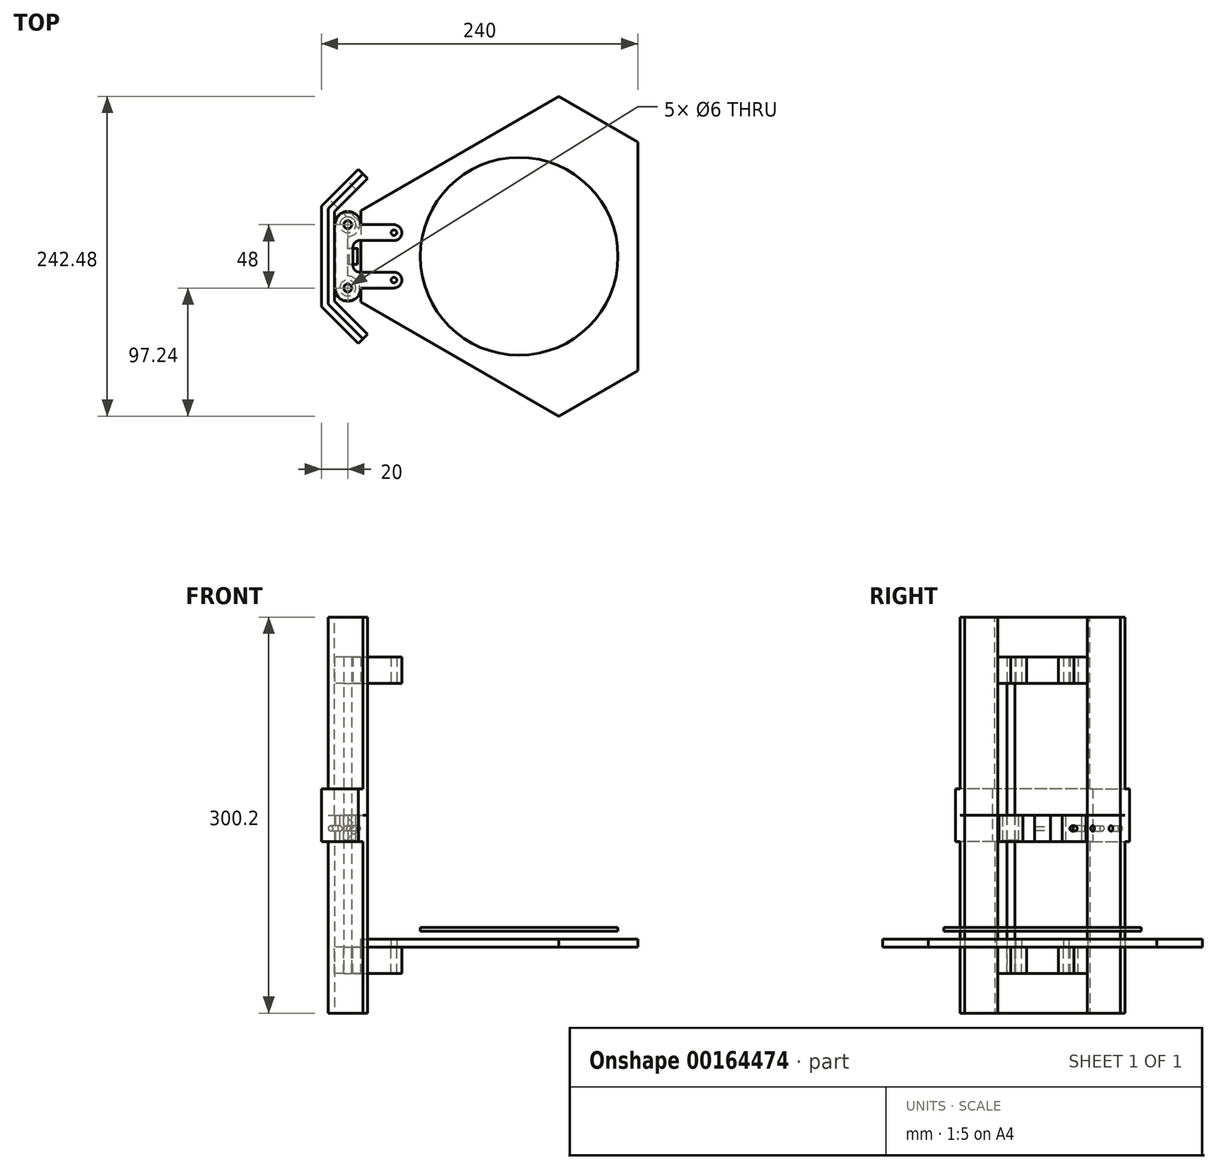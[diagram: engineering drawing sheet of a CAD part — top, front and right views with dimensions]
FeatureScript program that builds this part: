
annotation { "Feature Type Name" : "Feature", "Feature Type Description" : "" }
export const myFeature = defineFeature(function(context is Context, id is Id, definition is map)
    precondition{}
    {
        {
            var Q0;
            Q0=qCreatedBy(makeId("Top.planeOp"),FACE);
            var sketch = newSketch(context, id + "F0", { "sketchPlane" : qUnion([Q0])});
            skCircle(sketch, "E0", {"center": v(0, 0) * mm, "radius": 75 * mm});
            skSolve(sketch);
        }
        {
            var Q0;
            Q0=makeQuery(id+"F0.imprint","IMPRINT",FACE,{"disambiguationData":[TD([[makeQuery(id+"F0.imprint","IMPRINT",EDGE,{"derivedFrom":sQuery(id+"F0.wireOp",EDGE,"E0")}),1.0]])]});
            extrude(context, id + "F1", {"entities" : qUnion([Q0]), "depth" : 3 * mm});
        }
        {
            var Q0;
            Q0=qCreatedBy(makeId("Top.planeOp"),FACE);
            cPlane(context, id + "F2", {"entities" : qUnion([Q0]), "cplaneType" : CPlaneType.OFFSET, "offset" : 6 * mm, "oppositeDirection" : true, "width" : 150 * mm, "height" : 150 * mm});
        }
        {
            var Q0;
            Q0=qCreatedBy(id+"F2.planeOp",FACE);
            var sketch = newSketch(context, id + "F3", { "sketchPlane" : qUnion([Q0])});
            skLineSegment(sketch, "E1", {"start": v(30, 121.24) * mm, "end": v(-120, 34.64) * mm});
            skLineSegment(sketch, "E2", {"start": v(-120, 34.64) * mm, "end": v(-120, -34.64) * mm});
            skLineSegment(sketch, "E3", {"start": v(-120, 0) * mm, "end": v(0, 0) * mm, "construction": true});
            skLineSegment(sketch, "E4.1.0", {"start": v(30, -121.24) * mm, "end": v(90, -86.6) * mm});
            skLineSegment(sketch, "E4.1.1", {"start": v(-120, -34.64) * mm, "end": v(30, -121.24) * mm});
            skLineSegment(sketch, "E4.2.0", {"start": v(90, 86.6) * mm, "end": v(30, 121.24) * mm});
            skLineSegment(sketch, "E4.2.1", {"start": v(90, -86.6) * mm, "end": v(90, 86.6) * mm});
            skPoint(sketch, "E4.center", {"position": v(0, 0) * mm});
            skCircle(sketch, "E5", {"center": v(0, 0) * mm, "radius": 90 * mm, "construction": true});
            skSolve(sketch);
        }
        {
            var Q0;
            Q0=makeQuery(id+"F3.imprint","IMPRINT",FACE,{"disambiguationData":[TD([[makeQuery(id+"F3.imprint","IMPRINT",EDGE,{"derivedFrom":sQuery(id+"F3.wireOp",EDGE,"E1")}),1.0]])]});
            extrude(context, id + "F4", {"entities" : qUnion([Q0]), "oppositeDirection" : true, "depth" : 6 * mm});
        }
        {
            var Q0;
            Q0=makeQuery(id+"F4.opExtrude","CAP_FACE",FACE,{"disambiguationData":[OSD([sQuery(id+"F3.wireOp",EDGE,"E1"),sQuery(id+"F3.wireOp",EDGE,"E2"),sQuery(id+"F3.wireOp",EDGE,"E4.1.0"),sQuery(id+"F3.wireOp",EDGE,"E4.1.1"),sQuery(id+"F3.wireOp",EDGE,"E4.2.0"),sQuery(id+"F3.wireOp",EDGE,"E4.2.1")])],"isStart":false});
            var sketch = newSketch(context, id + "F5", { "sketchPlane" : qUnion([Q0])});
            skLineSegment(sketch, "E6", {"start": v(-120, 0) * mm, "end": v(-90, 0) * mm, "construction": true});
            skPoint(sketch, "E6.endSnap0", {"position": v(-120, 0) * mm});
            skLineSegment(sketch, "E7", {"start": v(-120, 18) * mm, "end": v(-95, 18) * mm, "construction": true});
            skArc(sketch, "E8.0.endCap", {"start": v(-95, 24) * mm, "mid": v(-89, 18) * mm, "end": v(-95, 12) * mm});
            skLineSegment(sketch, "E8.0.left", {"start": v(-120, 24) * mm, "end": v(-95, 24) * mm});
            skLineSegment(sketch, "E8.0.right", {"start": v(-119.48, 12) * mm, "end": v(-95, 12) * mm});
            skArc(sketch, "E9.MirrorCS", {"start": v(-95, -24) * mm, "mid": v(-89, -18) * mm, "end": v(-95, -12) * mm});
            skLineSegment(sketch, "E10.MirrorCS", {"start": v(-120, -24) * mm, "end": v(-95, -24) * mm});
            skLineSegment(sketch, "E11.MirrorCS", {"start": v(-119.48, -12) * mm, "end": v(-95, -12) * mm});
            skCircle(sketch, "E12", {"center": v(-95, 18) * mm, "radius": 2.1 * mm});
            skCircle(sketch, "E13", {"center": v(-95, -18) * mm, "radius": 2.1 * mm});
            skLineSegment(sketch, "E14", {"start": v(-140, 24) * mm, "end": v(-140, -24) * mm});
            skLineSegment(sketch, "E15", {"start": v(-126, 7) * mm, "end": v(-126, -7) * mm});
            skPoint(sketch, "E16.orphan", {"position": v(-120, -24) * mm});
            skPoint(sketch, "E17.MirrorCS.start.orphan", {"position": v(-119.48, -12) * mm});
            skLineSegment(sketch, "E18", {"start": v(-119.48, -12) * mm, "end": v(-121, -12) * mm});
            skLineSegment(sketch, "E19", {"start": v(-119.48, 12) * mm, "end": v(-121, 12) * mm});
            skArc(sketch, "E20", {"start": v(-121, 12) * mm, "mid": v(-124.54, 10.54) * mm, "end": v(-126, 7) * mm});
            skArc(sketch, "E21.MirrorCS", {"start": v(-121, -12) * mm, "mid": v(-124.54, -10.54) * mm, "end": v(-126, -7) * mm});
            skCircle(sketch, "E22", {"center": v(-130, -24) * mm, "radius": 3 * mm});
            skArc(sketch, "E23", {"start": v(-140, -24) * mm, "mid": v(-130, -34) * mm, "end": v(-120, -24) * mm});
            skCircle(sketch, "E24.MirrorC", {"center": v(-130, 24) * mm, "radius": 3 * mm});
            skArc(sketch, "E25.MirrorCS", {"start": v(-140, 24) * mm, "mid": v(-130, 34) * mm, "end": v(-120, 24) * mm});
            skSolve(sketch);
        }
        {
            var Q0;
            Q0 = qSketchRegion(id + "F5", true);
            extrude(context, id + "F6", {"entities" : qUnion([Q0]), "depth" : 20 * mm});
        }
        {
            var Q0;
            Q0=makeQuery(id+"F4.opExtrude","CAP_FACE",FACE,{"disambiguationData":[OSD([sQuery(id+"F3.wireOp",EDGE,"E1"),sQuery(id+"F3.wireOp",EDGE,"E2"),sQuery(id+"F3.wireOp",EDGE,"E4.1.0"),sQuery(id+"F3.wireOp",EDGE,"E4.1.1"),sQuery(id+"F3.wireOp",EDGE,"E4.2.0"),sQuery(id+"F3.wireOp",EDGE,"E4.2.1")])],"isStart":false});
            cPlane(context, id + "F7", {"entities" : qUnion([Q0]), "cplaneType" : CPlaneType.OFFSET, "offset" : 50 * mm, "width" : 150 * mm, "height" : 150 * mm});
        }
        {
            var Q0;
            Q0=qCreatedBy(id+"F7.planeOp",FACE);
            var sketch = newSketch(context, id + "F8", { "sketchPlane" : qUnion([Q0])});
            skLineSegment(sketch, "E26", {"start": v(-140, -34) * mm, "end": v(-140, 34) * mm});
            skLineSegment(sketch, "E27", {"start": v(-140, 34) * mm, "end": v(-115, 59) * mm});
            skLineSegment(sketch, "E28", {"start": v(-140, 0) * mm, "end": v(-105.12, 0) * mm, "construction": true});
            skLineSegment(sketch, "E29.MirrorCS", {"start": v(-140, -34) * mm, "end": v(-115, -59) * mm});
            skLineSegment(sketch, "E30.0", {"start": v(-145, 36.07) * mm, "end": v(-118.54, 62.54) * mm});
            skLineSegment(sketch, "E30.1", {"start": v(-145, -36.07) * mm, "end": v(-145, 36.07) * mm});
            skLineSegment(sketch, "E30.2", {"start": v(-145, -36.07) * mm, "end": v(-118.54, -62.54) * mm});
            skLineSegment(sketch, "E31", {"start": v(-115, 59) * mm, "end": v(-118.54, 62.54) * mm});
            skLineSegment(sketch, "E32", {"start": v(-115, -59) * mm, "end": v(-118.54, -62.54) * mm});
            skSolve(sketch);
        }
        {
            var Q0;
            Q0=makeQuery(id+"F8.imprint","IMPRINT",FACE,{"disambiguationData":[TD([[makeQuery(id+"F8.imprint","IMPRINT",EDGE,{"derivedFrom":sQuery(id+"F8.wireOp",EDGE,"E26")}),1.0]])]});
            extrude(context, id + "F9", {"entities" : qUnion([Q0]), "operationType" : NewBodyOperationType.ADD, "oppositeDirection" : true, "depth" : 150 * mm});
        }
        {
            var Q0;
            Q0=makeQuery(id+"F9.opExtrude","CAP_FACE",FACE,{"disambiguationData":[OSD([sQuery(id+"F8.wireOp",EDGE,"E26"),sQuery(id+"F8.wireOp",EDGE,"E27"),sQuery(id+"F8.wireOp",EDGE,"E29.MirrorCS"),sQuery(id+"F8.wireOp",EDGE,"E30.0"),sQuery(id+"F8.wireOp",EDGE,"E30.1"),sQuery(id+"F8.wireOp",EDGE,"E30.2"),sQuery(id+"F8.wireOp",EDGE,"E31"),sQuery(id+"F8.wireOp",EDGE,"E32")])],"isStart":false});
            cPlane(context, id + "F10", {"entities" : qUnion([Q0]), "cplaneType" : CPlaneType.OFFSET, "offset" : .1 * mm, "width" : 150 * mm, "height" : 150 * mm});
        }
        {
            var Q0;
            Q0=makeQuery(id+"F6.opExtrude","SWEPT_BODY",BODY,{"disambiguationData":[OSD([sQuery(id+"F5.wireOp",EDGE,"E8.0.endCap"),sQuery(id+"F5.wireOp",EDGE,"E8.0.left"),sQuery(id+"F5.wireOp",EDGE,"E8.0.right"),sQuery(id+"F5.wireOp",EDGE,"E9.MirrorCS"),sQuery(id+"F5.wireOp",EDGE,"E10.MirrorCS"),sQuery(id+"F5.wireOp",EDGE,"E11.MirrorCS"),sQuery(id+"F5.wireOp",EDGE,"E12"),sQuery(id+"F5.wireOp",EDGE,"E13"),sQuery(id+"F5.wireOp",EDGE,"E14"),sQuery(id+"F5.wireOp",EDGE,"E15"),sQuery(id+"F5.wireOp",EDGE,"E18"),sQuery(id+"F5.wireOp",EDGE,"E19"),sQuery(id+"F5.wireOp",EDGE,"E20"),sQuery(id+"F5.wireOp",EDGE,"E21.MirrorCS"),sQuery(id+"F5.wireOp",EDGE,"E22"),sQuery(id+"F5.wireOp",EDGE,"E23"),sQuery(id+"F5.wireOp",EDGE,"E24.MirrorC"),sQuery(id+"F5.wireOp",EDGE,"E25.MirrorCS")])]});
            var Q1;
            Q1=qCreatedBy(id+"F10.planeOp",FACE);
            mirror(context, id + "F11", {"entities" : qUnion([Q0]), "mirrorPlane" : qUnion([Q1])});
        }
        {
            var Q0;
            Q0=qCreatedBy(id+"F10.planeOp",FACE);
            var sketch = newSketch(context, id + "F12", { "sketchPlane" : qUnion([Q0])});
            skLineSegment(sketch, "E33.0", {"start": v(-150, -38.14) * mm, "end": v(-122.07, -66.07) * mm});
            skLineSegment(sketch, "E33.1", {"start": v(-150, 38.14) * mm, "end": v(-150, -38.14) * mm});
            skLineSegment(sketch, "E33.2", {"start": v(-150, 38.14) * mm, "end": v(-122.07, 66.07) * mm});
            skLineSegment(sketch, "E34.0", {"start": v(-145, -36.07) * mm, "end": v(-118.54, -62.54) * mm});
            skLineSegment(sketch, "E35.0", {"start": v(-145, 36.07) * mm, "end": v(-145, -36.07) * mm});
            skLineSegment(sketch, "E36.0", {"start": v(-145, 36.07) * mm, "end": v(-118.54, 62.54) * mm});
            skLineSegment(sketch, "E37", {"start": v(-122.07, -66.07) * mm, "end": v(-118.54, -62.54) * mm});
            skLineSegment(sketch, "E38", {"start": v(-122.07, 66.07) * mm, "end": v(-118.54, 62.54) * mm});
            skSolve(sketch);
        }
        {
            var Q0;
            Q0 = qSketchRegion(id + "F12", true);
            extrude(context, id + "F13", {"entities" : qUnion([Q0]), "operationType" : NewBodyOperationType.ADD, "endBound" : BoundingType.SYMMETRIC, "depth" : 40 * mm});
        }
        {
            var Q0;
            Q0=makeQuery(id+"F6.opExtrude","CAP_FACE",FACE,{"disambiguationData":[OSD([sQuery(id+"F5.wireOp",EDGE,"E8.0.endCap"),sQuery(id+"F5.wireOp",EDGE,"E8.0.left"),sQuery(id+"F5.wireOp",EDGE,"E8.0.right"),sQuery(id+"F5.wireOp",EDGE,"E9.MirrorCS"),sQuery(id+"F5.wireOp",EDGE,"E10.MirrorCS"),sQuery(id+"F5.wireOp",EDGE,"E11.MirrorCS"),sQuery(id+"F5.wireOp",EDGE,"E12"),sQuery(id+"F5.wireOp",EDGE,"E13"),sQuery(id+"F5.wireOp",EDGE,"E14"),sQuery(id+"F5.wireOp",EDGE,"E15"),sQuery(id+"F5.wireOp",EDGE,"E18"),sQuery(id+"F5.wireOp",EDGE,"E19"),sQuery(id+"F5.wireOp",EDGE,"E20"),sQuery(id+"F5.wireOp",EDGE,"E21.MirrorCS"),sQuery(id+"F5.wireOp",EDGE,"E22"),sQuery(id+"F5.wireOp",EDGE,"E23"),sQuery(id+"F5.wireOp",EDGE,"E24.MirrorC"),sQuery(id+"F5.wireOp",EDGE,"E25.MirrorCS")])],"isStart":false});
            var sketch = newSketch(context, id + "F14", { "sketchPlane" : qUnion([Q0])});
            skCircle(sketch, "E39.0", {"center": v(-130, 24) * mm, "radius": 3 * mm});
            skSolve(sketch);
        }
        {
            var Q0;
            Q0 = qSketchRegion(id + "F14", true);
            var Q1;
            Q1=makeQuery(id+"F11.opPattern","COPY",FACE,{"derivedFrom":makeQuery(id+"F6.opExtrude","CAP_FACE",FACE,{"disambiguationData":[OSD([sQuery(id+"F5.wireOp",EDGE,"E8.0.endCap"),sQuery(id+"F5.wireOp",EDGE,"E8.0.left"),sQuery(id+"F5.wireOp",EDGE,"E8.0.right"),sQuery(id+"F5.wireOp",EDGE,"E9.MirrorCS"),sQuery(id+"F5.wireOp",EDGE,"E10.MirrorCS"),sQuery(id+"F5.wireOp",EDGE,"E11.MirrorCS"),sQuery(id+"F5.wireOp",EDGE,"E12"),sQuery(id+"F5.wireOp",EDGE,"E13"),sQuery(id+"F5.wireOp",EDGE,"E14"),sQuery(id+"F5.wireOp",EDGE,"E15"),sQuery(id+"F5.wireOp",EDGE,"E18"),sQuery(id+"F5.wireOp",EDGE,"E19"),sQuery(id+"F5.wireOp",EDGE,"E20"),sQuery(id+"F5.wireOp",EDGE,"E21.MirrorCS"),sQuery(id+"F5.wireOp",EDGE,"E22"),sQuery(id+"F5.wireOp",EDGE,"E23"),sQuery(id+"F5.wireOp",EDGE,"E24.MirrorC"),sQuery(id+"F5.wireOp",EDGE,"E25.MirrorCS")])],"isStart":false}),"instanceName":"1"});
            extrude(context, id + "F15", {"entities" : qUnion([Q0]), "endBound" : BoundingType.UP_TO_SURFACE, "oppositeDirection" : true, "endBoundEntityFace" : qUnion([Q1]), "depth" : 25 * mm});
        }
        {
            var Q0;
            Q0=qCreatedBy(id+"F10.planeOp",FACE);
            var sketch = newSketch(context, id + "F16", { "sketchPlane" : qUnion([Q0])});
            skCircle(sketch, "E40", {"center": v(-130, -24) * mm, "radius": 6.05 * mm});
            skCircle(sketch, "E41", {"center": v(-130, -24) * mm, "radius": 3 * mm, "construction": true});
            skArc(sketch, "E42", {"start": v(-139, -24) * mm, "mid": v(-123.64, -30.36) * mm, "end": v(-130, -15) * mm});
            skLineSegment(sketch, "E43", {"start": v(-111.99, 0) * mm, "end": v(-93.99, 0) * mm});
            skArc(sketch, "E44.MirrorC", {"start": v(-139, 24) * mm, "mid": v(-123.64, 30.36) * mm, "end": v(-130, 15) * mm});
            skCircle(sketch, "E45.MirrorC", {"center": v(-130, 24) * mm, "radius": 6.05 * mm});
            skLineSegment(sketch, "E46", {"start": v(-139, -24) * mm, "end": v(-139, 24) * mm});
            skLineSegment(sketch, "E47.trimOffspring", {"start": v(-130, -15) * mm, "end": v(-130, 15) * mm});
            skSolve(sketch);
        }
        {
            var Q0;
            Q0=makeQuery(id+"F16.imprint","IMPRINT",FACE,{"disambiguationData":[TD([[makeQuery(id+"F16.imprint","IMPRINT",EDGE,{"derivedFrom":sQuery(id+"F16.wireOp",EDGE,"E40")}),-1.0]])]});
            extrude(context, id + "F17", {"entities" : qUnion([Q0]), "oppositeDirection" : true, "depth" : 20 * mm});
        }
        {
            var Q0;
            Q0=makeQuery(id+"F17.opExtrude","CAP_FACE",FACE,{"disambiguationData":[OSD([sQuery(id+"F16.wireOp",EDGE,"E40"),sQuery(id+"F16.wireOp",EDGE,"E42"),sQuery(id+"F16.wireOp",EDGE,"E44.MirrorC"),sQuery(id+"F16.wireOp",EDGE,"E45.MirrorC"),sQuery(id+"F16.wireOp",EDGE,"E46"),sQuery(id+"F16.wireOp",EDGE,"E47.trimOffspring")])],"isStart":true});
            var sketch = newSketch(context, id + "F18", { "sketchPlane" : qUnion([Q0])});
            skCircle(sketch, "E48", {"center": v(-130, -24) * mm, "radius": 3 * mm});
            skCircle(sketch, "E49", {"center": v(-130, -24) * mm, "radius": 6 * mm});
            skSolve(sketch);
        }
        {
            var Q0;
            Q0=makeQuery(id+"F18.imprint","IMPRINT",FACE,{"disambiguationData":[TD([[makeQuery(id+"F18.imprint","IMPRINT",EDGE,{"derivedFrom":sQuery(id+"F18.wireOp",EDGE,"E48")}),-1.0]])]});
            extrude(context, id + "F19", {"entities" : qUnion([Q0]), "oppositeDirection" : true, "depth" : 19 * mm});
        }
        {
            var Q0;
            Q0=makeQuery(id+"F13.opExtrude","SWEPT_FACE",FACE,{"disambiguationData":[OSD([sQuery(id+"F12.wireOp",EDGE,"E33.2")])]});
            var sketch = newSketch(context, id + "F20", { "sketchPlane" : qUnion([Q0])});
            skCircle(sketch, "E50", {"center": v(69.15, 78.05) * mm, "radius": 2.1 * mm});
            skLineSegment(sketch, "E51", {"start": v(69.15, 78.05) * mm, "end": v(49.55, 78.05) * mm, "construction": true});
            skCircle(sketch, "E52", {"center": v(49.55, 78.05) * mm, "radius": 2.1 * mm});
            skCircle(sketch, "E53", {"center": v(49.55, 78.05) * mm, "radius": 9.95 * mm, "construction": true});
            skCircle(sketch, "E54", {"center": v(69.15, 78.05) * mm, "radius": 9.95 * mm, "construction": true});
            skSolve(sketch);
        }
        {
            var Q0;
            Q0 = qSketchRegion(id + "F20", true);
            extrude(context, id + "F21", {"entities" : qUnion([Q0]), "operationType" : NewBodyOperationType.REMOVE, "endBound" : BoundingType.THROUGH_ALL, "oppositeDirection" : true, "depth" : 25 * mm});
        }
        {
            var Q0;
            Q0=qCreatedBy(makeId("Front.planeOp"),FACE);
            var sketch = newSketch(context, id + "F22", { "sketchPlane" : qUnion([Q0])});
            skCircle(sketch, "E55", {"center": v(-127, 78.1) * mm, "radius": 1.5 * mm});
            skCircle(sketch, "E56", {"center": v(-127, 78.1) * mm, "radius": 4.5 * mm});
            skLineSegment(sketch, "E57", {"start": v(-127, 78.1) * mm, "end": v(-130, 78.1) * mm, "construction": true});
            skSolve(sketch);
        }
        {
            var Q0;
            Q0 = qSketchRegion(id + "F22", true);
            extrude(context, id + "F23", {"entities" : qUnion([Q0]), "operationType" : NewBodyOperationType.ADD, "endBound" : BoundingType.SYMMETRIC, "depth" : 12 * mm});
        }
        {
            var Q0;
            Q0=makeQuery(id+"F23.boolean.opBoolean","INTERSECT",EDGE,{"disambiguationData":[OD(1.0)],"derivedFrom":[makeQuery(id+"F17.opExtrude","SWEPT_FACE",FACE,{"disambiguationData":[OSD([sQuery(id+"F16.wireOp",EDGE,"E47.trimOffspring")])]}),makeQuery(id+"F23.opExtrude","SWEPT_FACE",FACE,{"disambiguationData":[OSD([sQuery(id+"F22.wireOp",EDGE,"E56")])]})]});
            var Q1;
            Q1=makeQuery(id+"F23.boolean.opBoolean","INTERSECT",EDGE,{"disambiguationData":[OD(0.0)],"derivedFrom":[makeQuery(id+"F17.opExtrude","SWEPT_FACE",FACE,{"disambiguationData":[OSD([sQuery(id+"F16.wireOp",EDGE,"E47.trimOffspring")])]}),makeQuery(id+"F23.opExtrude","SWEPT_FACE",FACE,{"disambiguationData":[OSD([sQuery(id+"F22.wireOp",EDGE,"E56")])]})]});
            fillet(context, id + "F24", {"entities" : qUnion([Q0, Q1]), "radius" : 6 * mm, "tangentPropagation" : true, "allowEdgeOverflow" : false});
        }
        {
            var Q0;
            Q0=makeQuery(id+"F4.opExtrude","CAP_FACE",FACE,{"disambiguationData":[OSD([sQuery(id+"F3.wireOp",EDGE,"E1"),sQuery(id+"F3.wireOp",EDGE,"E2"),sQuery(id+"F3.wireOp",EDGE,"E4.1.0"),sQuery(id+"F3.wireOp",EDGE,"E4.1.1"),sQuery(id+"F3.wireOp",EDGE,"E4.2.0"),sQuery(id+"F3.wireOp",EDGE,"E4.2.1")])],"isStart":false});
            var sketch = newSketch(context, id + "F25", { "sketchPlane" : qUnion([Q0])});
            skCircle(sketch, "E58.0", {"center": v(-95, 18) * mm, "radius": 2.1 * mm});
            skCircle(sketch, "E59.0", {"center": v(-95, -18) * mm, "radius": 2.1 * mm});
            skSolve(sketch);
        }
        {
            var Q0;
            Q0 = qSketchRegion(id + "F25", true);
            extrude(context, id + "F26", {"entities" : qUnion([Q0]), "operationType" : NewBodyOperationType.REMOVE, "oppositeDirection" : true, "depth" : 25 * mm});
        }
        {
            var Q0;
            Q0=qCreatedBy(makeId("Right.planeOp"),FACE);
            var sketch = newSketch(context, id + "F27", { "sketchPlane" : qUnion([Q0])});
            skLineSegment(sketch, "E60", {"start": v(0, 0) * mm, "end": v(0, 66.25) * mm});
            skSolve(sketch);
        }
    });
